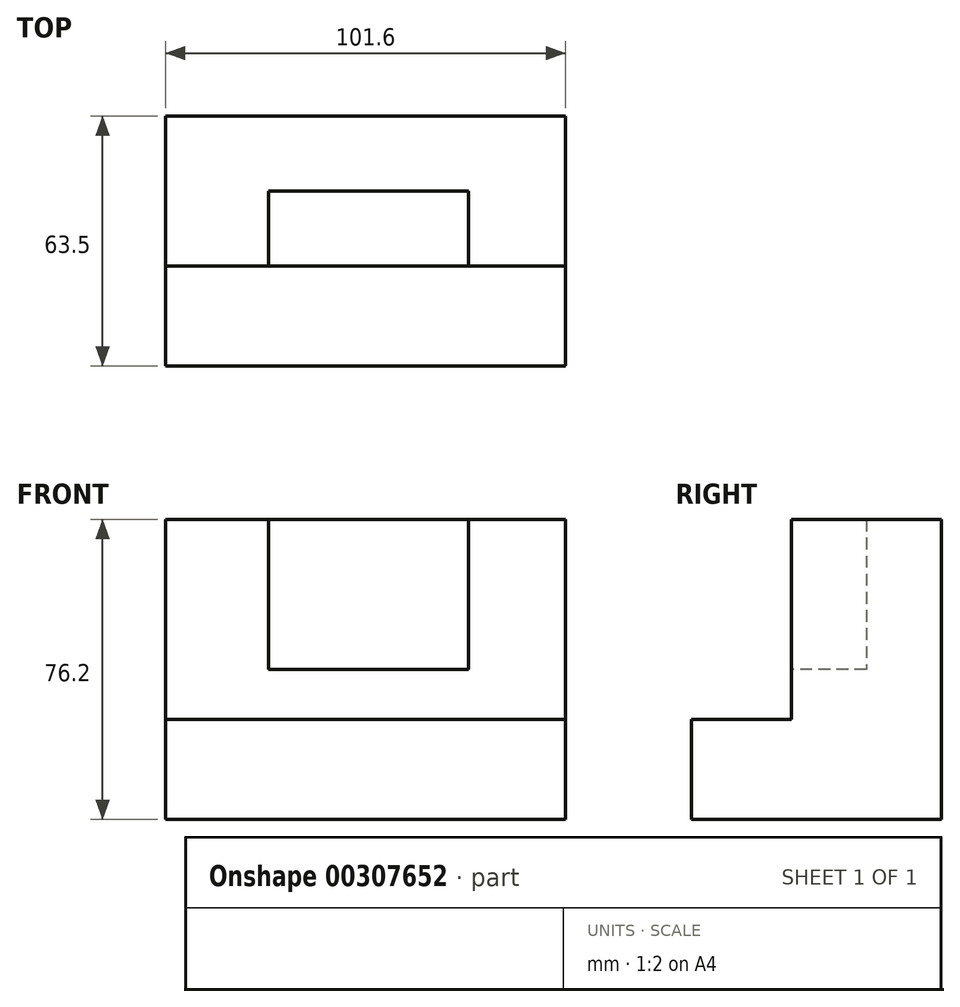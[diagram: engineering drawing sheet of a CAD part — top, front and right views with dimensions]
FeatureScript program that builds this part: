
annotation { "Feature Type Name" : "Feature", "Feature Type Description" : "" }
export const myFeature = defineFeature(function(context is Context, id is Id, definition is map)
    precondition{}
    {
        {
            var Q0;
            Q0=qCreatedBy(makeId("Right.planeOp"),FACE);
            var sketch = newSketch(context, id + "F0", { "sketchPlane" : qUnion([Q0])});
            skLineSegment(sketch, "E0", {"start": v(-49.08, -52.3) * mm, "end": v(14.42, -52.3) * mm});
            skLineSegment(sketch, "E1", {"start": v(14.42, -52.3) * mm, "end": v(14.42, 23.9) * mm});
            skLineSegment(sketch, "E2", {"start": v(14.42, 23.9) * mm, "end": v(-23.68, 23.9) * mm});
            skLineSegment(sketch, "E3", {"start": v(-23.68, 23.9) * mm, "end": v(-23.68, -26.9) * mm});
            skLineSegment(sketch, "E4", {"start": v(-23.68, -26.9) * mm, "end": v(-49.08, -26.9) * mm});
            skLineSegment(sketch, "E5", {"start": v(-49.08, -26.9) * mm, "end": v(-49.08, -52.3) * mm});
            skSolve(sketch);
        }
        {
            var Q0;
            Q0 = qSketchRegion(id + "F0", true);
            extrude(context, id + "F1", {"entities" : qUnion([Q0]), "depth" : 101.6 * mm});
        }
        {
            var Q0;
            Q0=makeQuery(id+"F1.opExtrude","SWEPT_FACE",FACE,{"disambiguationData":[OSD([sQuery(id+"F0.wireOp",EDGE,"E3")])]});
            var sketch = newSketch(context, id + "F2", { "sketchPlane" : qUnion([Q0])});
            skLineSegment(sketch, "E6", {"start": v(26.16, 23.9) * mm, "end": v(26.16, -14.2) * mm});
            skLineSegment(sketch, "E7", {"start": v(26.16, -14.2) * mm, "end": v(76.96, -14.2) * mm});
            skLineSegment(sketch, "E8", {"start": v(76.96, -14.2) * mm, "end": v(76.96, 23.9) * mm});
            skLineSegment(sketch, "E9", {"start": v(76.96, 23.9) * mm, "end": v(26.16, 23.9) * mm});
            skSolve(sketch);
        }
        {
            var Q0;
            Q0=makeQuery(id+"F2.imprint","IMPRINT",FACE,{"disambiguationData":[TD([[makeQuery(id+"F2.imprint","IMPRINT",EDGE,{"derivedFrom":sQuery(id+"F2.wireOp",EDGE,"E6")}),1.0]])]});
            extrude(context, id + "F3", {"entities" : qUnion([Q0]), "operationType" : NewBodyOperationType.REMOVE, "oppositeDirection" : true, "depth" : 19.05 * mm});
        }
    });
